# Revit family: CENTUM Adapterhalter quer
name_source: partatom
category: HLS-Bauteile
revit_build: Autodesk Revit 2017 (Build: 20190507_1515(x64)
units: mm (PartAtom-declared; Revit-internal decimal feet)

## family parameters
Arbeitsebenenbasiert = Ja
Beim Laden mit Abzugskörper schneiden = Nein
Bemaßung runder Anschluss = Durchmesser verwenden
Gemeinsam genutzt = Ja
Immer vertikal = Nein
Raumberechnungspunkt = Nein
Teiletyp = Normal

## types (1)
- CENTUM Adapterhalter quer
    Artikelnummer = 1621005021
    Ausrichtung Profil = quer
    EAN = 4250928448200
    Fabrikat = MEFA
    Firma = MEFA Befestigungs- und Montagesysteme GmbH
    Gewicht = 2.32 kg
    Gewicht pro Bauteil = 2.32 kg
    Grenzmoment fbv = 0,8 Nm
    Grenzmoment fsv = 0,35 Nm
    Höhe Profil = 90 mm  [stored 0.295276 ft]
    Kurztext1 = Adapterhalter CENTUM C-Profil 45
    Kurztext2 = Profilausrichtung quer Profilhöhe 90 mm
    Länge = 130 mm  [stored 0.426509 ft]
    Material = Stahl
    Materialname = S235
    Mengeneinheit = St
    Oberflaeche = feuerstückverzinkt
    Profiltyp = XL 100, XL 200
    Sicherheitsfaktor = 1.54
    Stärke = 6 mm  [stored 0.019685 ft]
    Vorgabe-Ansicht = 1219 mm
    max. zul. Last = 12.00 kN
    vpe = 1 St

note: [stored X ft] marks values corroborated as IEEE doubles in the binary element streams (Revit-internal decimal feet)
